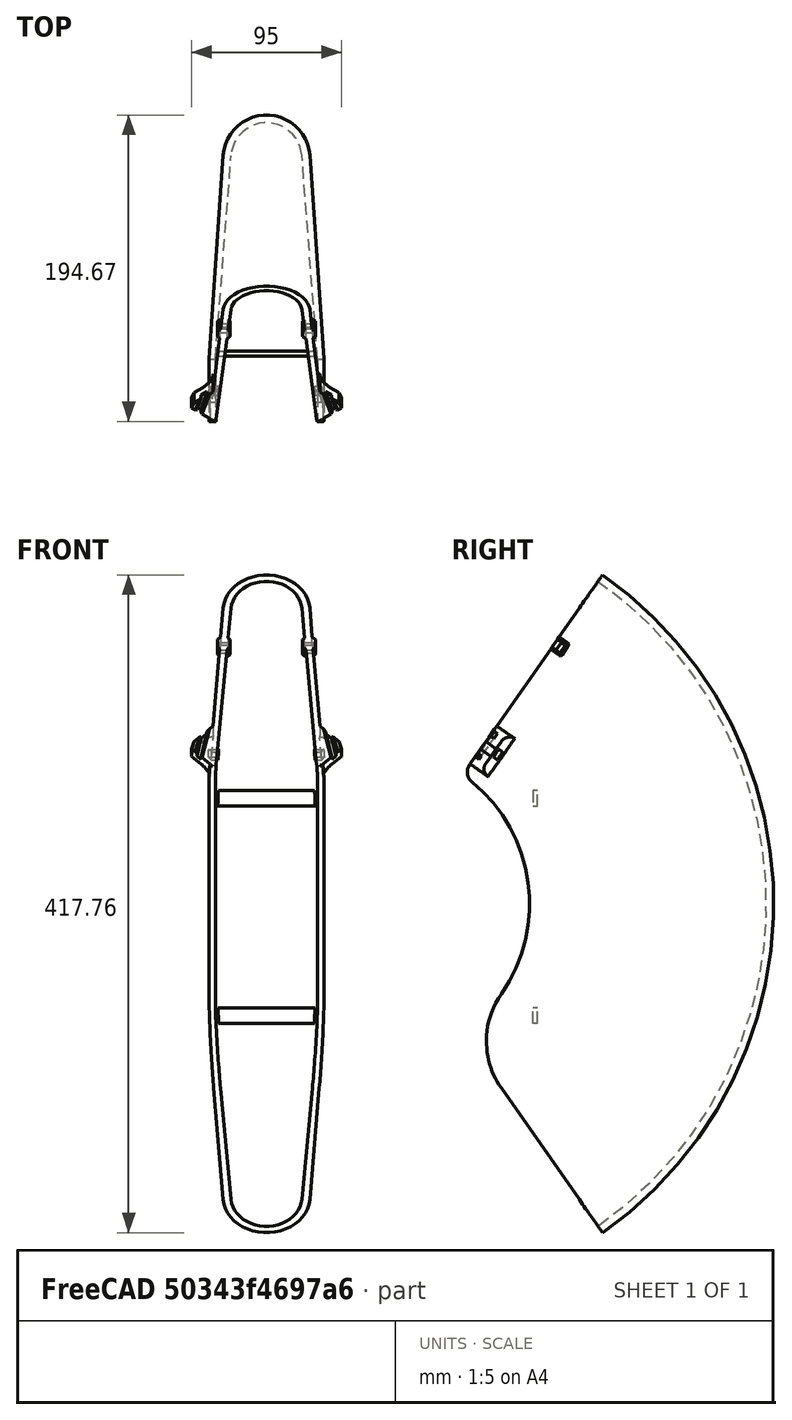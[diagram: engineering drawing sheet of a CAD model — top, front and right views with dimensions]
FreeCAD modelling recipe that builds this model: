
FCSTD DOCUMENT  (FreeCAD 0.19R)
Label: Mudguard4.2FCStd
License: All rights reserved
LicenseURL: http://en.wikipedia.org/wiki/All_rights_reserved
objects: Sketcher::SketchObject×4, PartDesign::Fillet×3, Part::Box×2, PartDesign::Pocket×2, PartDesign::Revolution×1, PartDesign::ShapeBinder×1, PartDesign::Pad×1, Part::Cylinder×1, PartDesign::Chamfer×1, PartDesign::Body×1, Part::Cut×1, Part::MultiFuse×1, Mesh::Feature×1
note: 27 computed .brp shape members not serialized (recipe doc carries the construction recipe); baked Part::Feature solids carry a one-line shape summary decoded from their .brp

FEATURE [Sketcher::SketchObject] Sketch
  FullyConstrained = false
  MapMode = 5
  Support = -> [XY_Plane]
  sketch-geometry (9):
    g0: LineSegment StartX=-38.02 StartY=255 StartZ=0 EndX=36.46 EndY=255 EndZ=0
    g1: ArcOfCircle CenterX=1e-15 CenterY=227.426 CenterZ=0 NormalX=0 NormalY=0 NormalZ=1 AngleXU=0 Radius=27.5737 StartAngle=0.0694168 EndAngle=3.07218
    g2: ArcOfCircle CenterX=0 CenterY=227.499 CenterZ=0 NormalX=0 NormalY=0 NormalZ=1 AngleXU=0 Radius=22.5673 StartAngle=0.0772218 EndAngle=3.06437
    g3: LineSegment StartX=-36.5 StartY=100 StartZ=0 EndX=-27.5073 EndY=229.339 EndZ=0
    g4: LineSegment StartX=-32.5 StartY=100 StartZ=0 EndX=-22.5 EndY=229.24 EndZ=0
    g5: LineSegment StartX=22.5 StartY=229.24 StartZ=0 EndX=32.5 EndY=100 EndZ=0
    g6: LineSegment StartX=-36.5 StartY=100 StartZ=0 EndX=-32.5 EndY=100 EndZ=0
    g7: LineSegment StartX=32.5 StartY=100 StartZ=0 EndX=36.5 EndY=100 EndZ=0
    g8: LineSegment StartX=36.5 StartY=100 StartZ=0 EndX=27.5073 EndY=229.339 EndZ=0
  constraints (23):
    c: Horizontal(g0)
    c: DistanceY(g0) = 255
    c: Tangent(g1,g0)
    c: Symmetric(g1,g1,g-2)
    c: Distance(g0) = 74.48
    c: DistanceX(g0) = 36.46
    c: Tangent(g3,g1) = 1.5708
    c: Coincident(g6,g3)
    c: Coincident(g6,g4)
    c: Distance(g6) = 4
    c: Tangent(g4,g2) = 1.5708
    c: Tangent(g5,g2) = 1.5708
    c: PointOnObject(g2,g-2)
    c: Coincident(g5,g7)
    c: Coincident(g7,g8)
    c: Coincident(g8,g1)
    c: Symmetric(g5,g4,g-2)
    c: Symmetric(g7,g3,g-2)
    c: Horizontal(g7)
    c: Distance(g5,g4) = 65
    c: Distance(g2,g2) = 45
    c: Distance(g1,g5) = 5
    c: DistanceY(g7) = 100
FEATURE [PartDesign::Revolution] Revolution
  Angle = 110
  Axis = (1,0,0)
  Base = (0,0,0)
  Midplane = true
  Profile = -> Sketch
  ReferenceAxis = -> Sketch [H_Axis]
FEATURE [PartDesign::ShapeBinder] CopyFusion
  Placement = pos=(0,0,0) rot=(1,0,0;0.785398rad)
  TraceSupport = false
FEATURE [Part::Box] Box002  label="Cube002"
  AttacherType = Attacher::AttachEngine3D
  Height = 10
  Length = 67
  Placement = pos=(-34,102,-76) rot=(0,0,1;0rad)
  Width = 3
FEATURE [Part::Box] Box003  label="Cube003"
  AttacherType = Attacher::AttachEngine3D
  Height = 10
  Length = 68
  Placement = pos=(-34,102,62) rot=(0,0,1;0rad)
  Width = 3
FEATURE [PartDesign::Fillet] Fillet
  Base = -> Revolution [Edge7,Edge19]
  BaseFeature = -> Revolution
  Radius = 8
  SupportTransform = false
FEATURE [PartDesign::Fillet] Fillet001
  Base = -> Fillet [Edge7,Edge14]
  BaseFeature = -> Fillet
  Radius = 52
  SupportTransform = false
FEATURE [Sketcher::SketchObject] Sketch002
  ExternalGeometry = -> [Fillet001]
  FullyConstrained = true
  MapMode = 5
  Placement = pos=(0,1.16e-14,-8.2e-15) rot=(1,0,0;0.959931rad)
  Support = -> [Fillet001]
  sketch-geometry (21):
    g0: LineSegment StartX=-29.785 StartY=255 StartZ=0 EndX=29.785 EndY=255 EndZ=0
    g1: LineSegment StartX=-45.9471 StartY=125.796 StartZ=0 EndX=-47.5 EndY=120 EndZ=0
    g2: LineSegment StartX=-47.5 StartY=120 StartZ=0 EndX=-34.2488 EndY=106.749 EndZ=0
    g3: LineSegment StartX=-34.2488 StartY=106.749 StartZ=0 EndX=-30 EndY=141.743 EndZ=0
    g4: LineSegment StartX=-30 StartY=141.743 StartZ=0 EndX=-45.9471 EndY=125.796 EndZ=0
    g5: LineSegment StartX=45.9471 StartY=125.796 StartZ=0 EndX=47.5 EndY=120 EndZ=0
    g6: LineSegment StartX=47.5 StartY=120 StartZ=0 EndX=34.2488 EndY=106.749 EndZ=0
    g7: LineSegment StartX=34.2488 StartY=106.749 StartZ=0 EndX=30 EndY=141.743 EndZ=0
    g8: LineSegment StartX=30 StartY=141.743 StartZ=0 EndX=45.9471 EndY=125.796 EndZ=0
    g9: LineSegment StartX=27 StartY=195 StartZ=0 EndX=31 EndY=199 EndZ=0
    g10: LineSegment StartX=31 StartY=199 StartZ=0 EndX=31 EndY=205 EndZ=0
    g11: LineSegment StartX=31 StartY=205 StartZ=0 EndX=27 EndY=209 EndZ=0
    g12: LineSegment StartX=27 StartY=209 StartZ=0 EndX=23 EndY=205 EndZ=0
    g13: LineSegment StartX=23 StartY=205 StartZ=0 EndX=23 EndY=199 EndZ=0
    g14: LineSegment StartX=23 StartY=199 StartZ=0 EndX=27 EndY=195 EndZ=0
    g15: LineSegment StartX=-27 StartY=195 StartZ=0 EndX=-23 EndY=199 EndZ=0
    g16: LineSegment StartX=-23 StartY=199 StartZ=0 EndX=-23 EndY=205 EndZ=0
    g17: LineSegment StartX=-23 StartY=205 StartZ=0 EndX=-27 EndY=209 EndZ=0
    g18: LineSegment StartX=-27 StartY=209 StartZ=0 EndX=-31 EndY=205 EndZ=0
    g19: LineSegment StartX=-31 StartY=205 StartZ=0 EndX=-31 EndY=199 EndZ=0
    g20: LineSegment StartX=-31 StartY=199 StartZ=0 EndX=-27 EndY=195 EndZ=0
  constraints (56):
    c: Coincident(g1,g2)
    c: Coincident(g2,g3)
    c: Coincident(g3,g4)
    c: Coincident(g4,g1)
    c: Coincident(g5,g6)
    c: Coincident(g6,g7)
    c: Coincident(g7,g8)
    c: Coincident(g8,g5)
    c: Symmetric(g7,g3,g-2)
    c: Symmetric(g6,g2,g-2)
    c: Equal(g5,g1)
    c: Symmetric(g5,g1,g-2)
    c: Equal(g2,g6)
    c: Distance(g5,g1) = 95
    c: Angle(g6) = -2.35619
    c: Coincident(g9,g10)
    c: Vertical(g10)
    c: Coincident(g10,g11)
    c: Coincident(g11,g12)
    c: Coincident(g12,g13)
    c: Vertical(g13)
    c: Coincident(g13,g14)
    c: Coincident(g14,g9)
    c: Coincident(g15,g16)
    c: Coincident(g16,g17)
    c: Coincident(g17,g18)
    c: Coincident(g18,g19)
    c: Coincident(g19,g20)
    c: Coincident(g20,g15)
    c: Distance(g5) = 6
    c: Angle(g5) = -1.309
    c: Symmetric(g0,g0,g-2)
    c: Distance(g0) = 59.57
    c: Tangent(g0,g-3)
    c: Angle(g8) = -0.785398
    c: Distance(g7,g3) = 60
    c: Distance(g9,g13) = 8
    c: Symmetric(g13,g15,g-2)
    c: Symmetric(g12,g16,g-2)
    c: Symmetric(g9,g19,g-2)
    c: Symmetric(g10,g18,g-2)
    c: Equal(g13,g19)
    c: Distance(g10) = 6
    c: Angle(g12,g11) = 1.5708
    c: Equal(g18,g12)
    c: Equal(g20,g14)
    c: Equal(g15,g9)
    c: Equal(g17,g11)
    c: Angle(g15,g20) = 1.5708
    c: Equal(g20,g15)
    c: Distance(g10,g0) = 50
    c: DistanceY(g12,g10) = 0
    c: Distance(g9,g19) = 62
    c: Distance(g5,g0) = 135
    c: Distance(g2) = 18.74
    c: Equal(g17,g18)
FEATURE [PartDesign::Pad] Pad001
  BaseFeature = -> Fillet001
  Direction = (1,1,1)
  Length = 8
  Length2 = 8
  Profile = -> Sketch002
  Reversed = true
  Type = 0
FEATURE [Sketcher::SketchObject] Sketch003
  FullyConstrained = true
  MapMode = 5
  Placement = pos=(0,2.33e-14,-1.63e-14) rot=(1,0,0;0.959931rad)
  Support = -> [Pad001]
  sketch-geometry (8):
    g0: LineSegment StartX=35 StartY=146.87 StartZ=0 EndX=45 EndY=97.88 EndZ=0
    g1: LineSegment StartX=45 StartY=97.88 StartZ=0 EndX=47.9394 EndY=98.48 EndZ=0
    g2: LineSegment StartX=47.9394 StartY=98.48 StartZ=0 EndX=37.9394 EndY=147.47 EndZ=0
    g3: LineSegment StartX=37.9394 StartY=147.47 StartZ=0 EndX=35 EndY=146.87 EndZ=0
    g4: LineSegment StartX=-47.9394 StartY=98.48 StartZ=0 EndX=-45 EndY=97.88 EndZ=0
    g5: LineSegment StartX=-45 StartY=97.88 StartZ=0 EndX=-35 EndY=146.87 EndZ=0
    g6: LineSegment StartX=-47.9394 StartY=98.48 StartZ=0 EndX=-37.9394 EndY=147.47 EndZ=0
    g7: LineSegment StartX=-37.9394 StartY=147.47 StartZ=0 EndX=-35 EndY=146.87 EndZ=0
  constraints (22):
    c: Coincident(g0,g1)
    c: Coincident(g1,g2)
    c: Coincident(g2,g3)
    c: Coincident(g3,g0)
    c: Coincident(g4,g5)
    c: Equal(g1,g3)
    c: Equal(g0,g2)
    c: Symmetric(g4,g0,g-2)
    c: Perpendicular(g0,g1)
    c: Distance(g3) = 3
    c: Distance(g0,g4) = 90
    c: Coincident(g4,g6)
    c: Coincident(g6,g7)
    c: Coincident(g7,g5)
    c: Equal(g7,g3)
    c: Equal(g6,g5)
    c: Perpendicular(g6,g7)
    c: Symmetric(g0,g5,g-2)
    c: Distance(g2) = 50
    c: Equal(g4,g7)
    c: DistanceY(g0) = 97.88
    c: Distance(g5,g0) = 70
FEATURE [Part::Cylinder] Cylinder
  Angle = 360
  AttacherType = Attacher::AttachEngine3D
  Height = 20
  Placement = pos=(33,99,209) rot=(0,-0.999201,0.039968;1.5708rad)
  Radius = 10
FEATURE [PartDesign::Pocket] Pocket
  BaseFeature = -> Pad001
  Length = 3
  Length2 = 100
  Profile = -> Sketch003
  Type = 0
FEATURE [PartDesign::Chamfer] Chamfer
  Angle = 45
  Base = -> Pocket [Edge155,Edge113,Edge162,Edge165]
  BaseFeature = -> Pocket
  ChamferType = 0
  FlipDirection = false
  Size = 1
  Size2 = 1
  SupportTransform = false
FEATURE [PartDesign::Fillet] Fillet002
  Base = -> Chamfer [Edge24,Edge103]
  BaseFeature = -> Chamfer
  Radius = 6
  SupportTransform = false
FEATURE [Sketcher::SketchObject] Sketch004
  FullyConstrained = false
  MapMode = 5
  Placement = pos=(-31,0,0) rot=(0.57735,-0.57735,-0.57735;2.0944rad)
  Support = -> [Fillet002]
  sketch-geometry (8):
    g0: LineSegment StartX=-122.627 StartY=164.31 StartZ=0 EndX=-119.228 EndY=159.366 EndZ=0
    g1: LineSegment StartX=-119.228 StartY=159.366 StartZ=0 EndX=-116.756 EndY=161.065 EndZ=0
    g2: LineSegment StartX=-116.756 StartY=161.065 StartZ=0 EndX=-120.154 EndY=166.009 EndZ=0
    g3: LineSegment StartX=-120.154 StartY=166.009 StartZ=0 EndX=-122.627 EndY=164.31 EndZ=0
    g4: LineSegment StartX=-76.9755 StartY=93.1865 StartZ=0 EndX=-79.4599 EndY=91.5049 EndZ=0
    g5: LineSegment StartX=-79.4599 StartY=91.5049 StartZ=0 EndX=-82.8231 EndY=96.4737 EndZ=0
    g6: LineSegment StartX=-82.8231 StartY=96.4737 StartZ=0 EndX=-80.3387 EndY=98.1553 EndZ=0
    g7: LineSegment StartX=-80.3387 StartY=98.1553 StartZ=0 EndX=-76.9755 EndY=93.1865 EndZ=0
  constraints (18):
    c: Coincident(g0,g1)
    c: Coincident(g1,g2)
    c: Coincident(g2,g3)
    c: Coincident(g3,g0)
    c: Coincident(g4,g5)
    c: Coincident(g5,g6)
    c: Coincident(g6,g7)
    c: Coincident(g7,g4)
    c: Equal(g1,g3)
    c: Equal(g3,g6)
    c: Equal(g6,g4)
    c: Distance(g6) = 3
    c: Perpendicular(g0,g3)
    c: Equal(g2,g0)
    c: Equal(g0,g5)
    c: Equal(g5,g7)
    c: Distance(g0) = 6
    c: Perpendicular(g5,g4)
FEATURE [PartDesign::Pocket] Pocket001
  BaseFeature = -> Fillet002
  Length = 150
  Length2 = 100
  Profile = -> Sketch004
  Type = 4
FEATURE [PartDesign::Body] Body
  Group = -> [Sketch,Revolution,CopyFusion,Fillet,Fillet001,Sketch002,Pad001,Sketch003,Sketch004,Pocket,Chamfer,Fillet002,Pocket001]
  Origin = -> Origin
  Tip = -> Pocket001
FEATURE [Part::Cut] Cut
  Base = -> Pocket001
  Tool = -> Cylinder
FEATURE [Part::MultiFuse] Fusion
  Shapes = -> [Box003,Box002,Cut]
FEATURE [Mesh::Feature] Mesh  label="Fusion (Meshed)"
